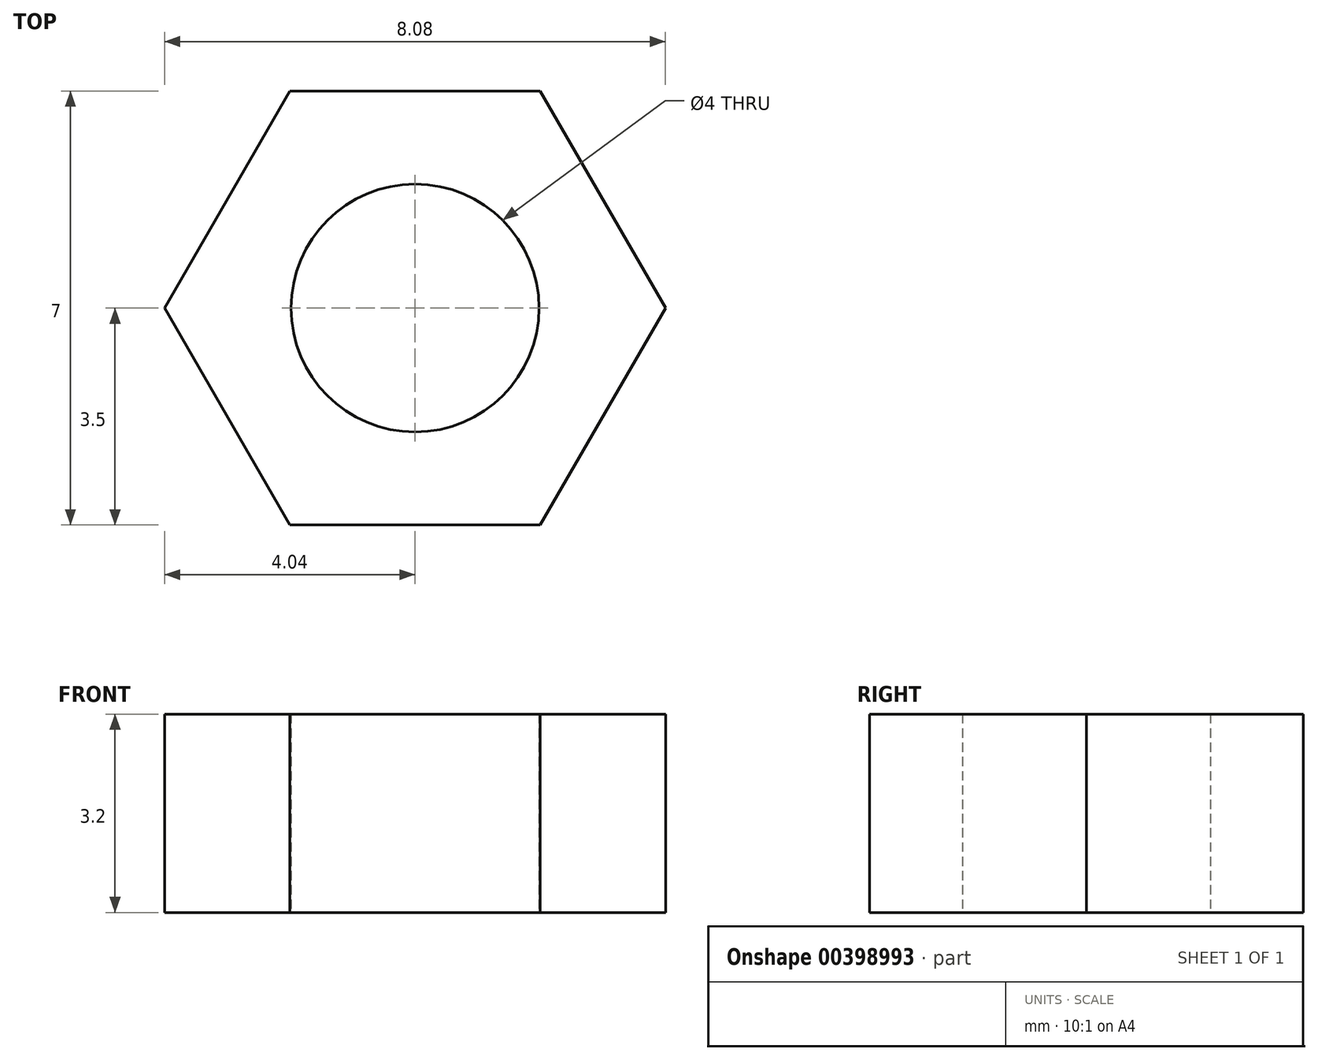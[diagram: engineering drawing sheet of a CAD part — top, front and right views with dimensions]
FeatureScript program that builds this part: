
annotation { "Feature Type Name" : "Feature", "Feature Type Description" : "" }
export const myFeature = defineFeature(function(context is Context, id is Id, definition is map)
    precondition{}
    {
        {
            var Q0;
            Q0=qCreatedBy(makeId("Top.planeOp"),FACE);
            var sketch = newSketch(context, id + "F0", { "sketchPlane" : qUnion([Q0])});
            skCircle(sketch, "E0.cCircle", {"center": v(0, 0) * mm, "radius": 3.5 * mm, "construction": true});
            skLineSegment(sketch, "E0.0", {"start": v(2.02, -3.5) * mm, "end": v(-2.02, -3.5) * mm});
            skLineSegment(sketch, "E0.1", {"start": v(-2.02, -3.5) * mm, "end": v(-4.04, 0) * mm});
            skLineSegment(sketch, "E0.2", {"start": v(-4.04, 0) * mm, "end": v(-2.02, 3.5) * mm});
            skLineSegment(sketch, "E0.3", {"start": v(-2.02, 3.5) * mm, "end": v(2.02, 3.5) * mm});
            skLineSegment(sketch, "E0.4", {"start": v(2.02, 3.5) * mm, "end": v(4.04, 0) * mm});
            skLineSegment(sketch, "E0.5", {"start": v(4.04, 0) * mm, "end": v(2.02, -3.5) * mm});
            skPoint(sketch, "E0.0.midPoint", {"position": v(0, -3.5) * mm});
            skCircle(sketch, "E1", {"center": v(0, 0) * mm, "radius": 2 * mm});
            skSolve(sketch);
        }
        {
            var Q0;
            Q0=qSketchRegion(id+"F0",true);
            extrude(context, id + "F1", {"entities" : qUnion([Q0]), "depth" : 3.2 * mm});
        }
    });
